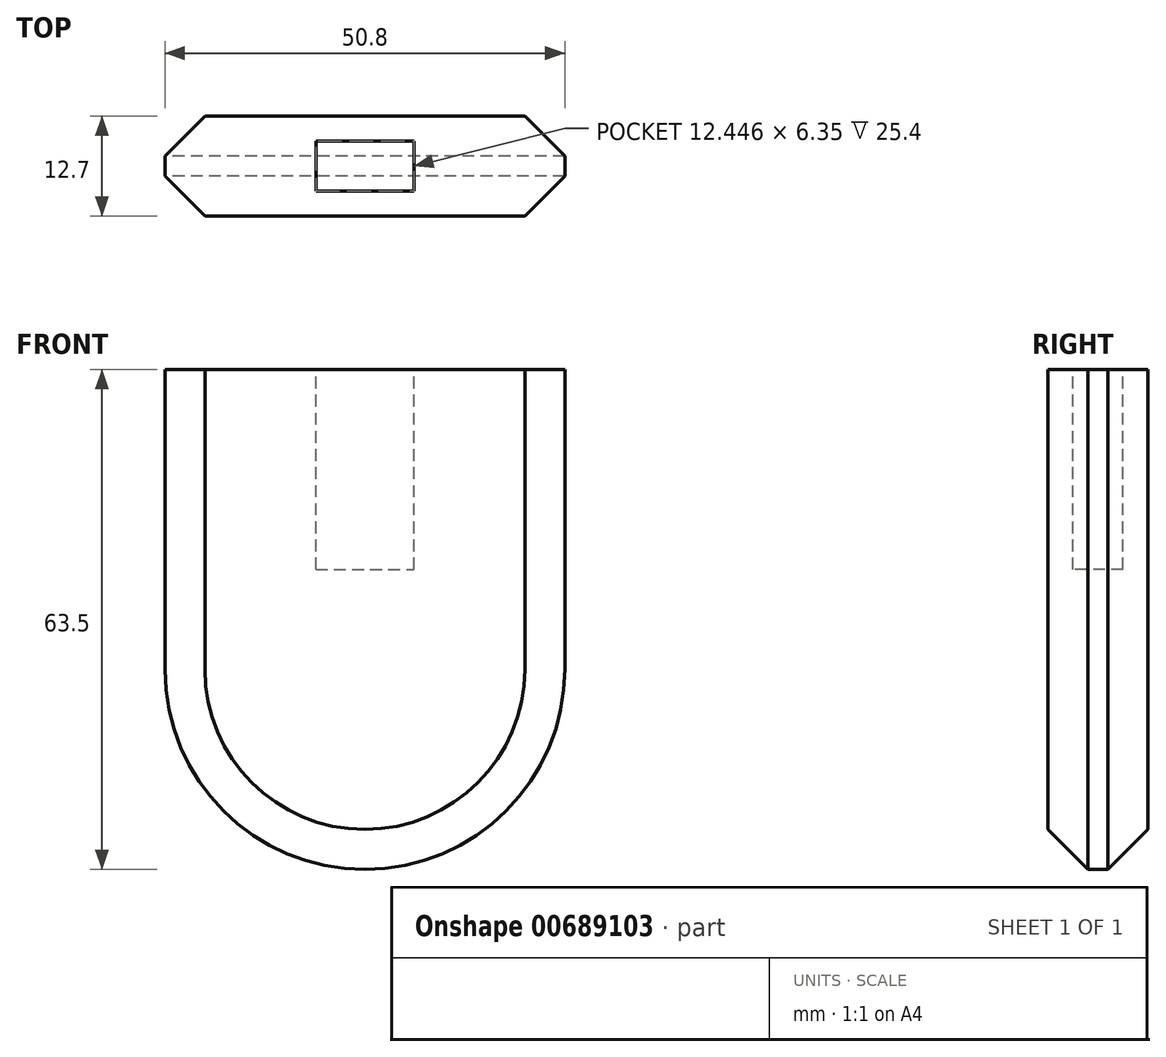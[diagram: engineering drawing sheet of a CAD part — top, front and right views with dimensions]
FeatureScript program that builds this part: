
annotation { "Feature Type Name" : "Feature", "Feature Type Description" : "" }
export const myFeature = defineFeature(function(context is Context, id is Id, definition is map)
    precondition{}
    {
        {
            var Q0;
            Q0=qCreatedBy(makeId("Top.planeOp"),FACE);
            var sketch = newSketch(context, id + "F0", { "sketchPlane" : qUnion([Q0])});
            skLineSegment(sketch, "E0.bottom", {"start": v(-25.4, 6.35) * mm, "end": v(25.4, 6.35) * mm});
            skLineSegment(sketch, "E0.top", {"start": v(-25.4, -6.35) * mm, "end": v(25.4, -6.35) * mm});
            skLineSegment(sketch, "E0.left", {"start": v(-25.4, 6.35) * mm, "end": v(-25.4, -6.35) * mm});
            skLineSegment(sketch, "E0.right", {"start": v(25.4, 6.35) * mm, "end": v(25.4, -6.35) * mm});
            skPoint(sketch, "E0.middle", {"position": v(0, 0) * mm});
            skSolve(sketch);
        }
        {
            var Q0;
            Q0 = qSketchRegion(id + "F0", true);
            extrude(context, id + "F1", {"entities" : qUnion([Q0]), "depth" : 25.4 * mm, "offsetDistance" : 25.4 * mm});
        }
        {
            var Q0;
            Q0 = qSketchRegion(id + "F0", true);
            extrude(context, id + "F2", {"entities" : qUnion([Q0]), "operationType" : NewBodyOperationType.ADD, "depth" : 63.5 * mm, "offsetDistance" : 25.4 * mm});
        }
        {
            var Q0;
            Q0=makeQuery(id+"F1.opExtrude","CAP_EDGE",EDGE,{"disambiguationData":[OSD([sQuery(id+"F0.wireOp",EDGE,"E0.right")])],"isStart":true});
            var Q1;
            Q1=makeQuery(id+"F1.opExtrude","CAP_EDGE",EDGE,{"disambiguationData":[OSD([sQuery(id+"F0.wireOp",EDGE,"E0.left")])],"isStart":true});
            fillet(context, id + "F3", {"entities" : qUnion([Q0, Q1]), "radius" : 25.4 * mm, "tangentPropagation" : true, "allowEdgeOverflow" : false});
        }
        {
            var Q0;
            {var subQ0=sQuery(id+"F0.wireOp",EDGE,"E0.top");Q0=makeQuery(id+"F3.opFillet","BLEND_EDGE",EDGE,{"blendedFrom":[makeQuery(id+"F1.opExtrude","CAP_EDGE",EDGE,{"disambiguationData":[OSD([sQuery(id+"F0.wireOp",EDGE,"E0.left")])],"isStart":true}),makeQuery(id+"F2.boolean.opBoolean","MERGE",FACE,{"derivedFrom":[makeQuery(id+"F1.opExtrude","SWEPT_FACE",FACE,{"disambiguationData":[OSD([subQ0])]}),makeQuery(id+"F2.opExtrude","SWEPT_FACE",FACE,{"disambiguationData":[OSD([subQ0])]})]})],"blendedInto":[makeQuery(id+"F2.boolean.opBoolean","MERGE",FACE,{"derivedFrom":[makeQuery(id+"F1.opExtrude","SWEPT_FACE",FACE,{"disambiguationData":[OSD([subQ0])]}),makeQuery(id+"F2.opExtrude","SWEPT_FACE",FACE,{"disambiguationData":[OSD([subQ0])]})]})]});}
            var Q1;
            {var subQ0=sQuery(id+"F0.wireOp",EDGE,"E0.bottom");Q1=makeQuery(id+"F3.opFillet","BLEND_EDGE",EDGE,{"blendedFrom":[makeQuery(id+"F1.opExtrude","CAP_EDGE",EDGE,{"disambiguationData":[OSD([sQuery(id+"F0.wireOp",EDGE,"E0.left")])],"isStart":true}),makeQuery(id+"F2.boolean.opBoolean","MERGE",FACE,{"derivedFrom":[makeQuery(id+"F1.opExtrude","SWEPT_FACE",FACE,{"disambiguationData":[OSD([subQ0])]}),makeQuery(id+"F2.opExtrude","SWEPT_FACE",FACE,{"disambiguationData":[OSD([subQ0])]})]})],"blendedInto":[makeQuery(id+"F2.boolean.opBoolean","MERGE",FACE,{"derivedFrom":[makeQuery(id+"F1.opExtrude","SWEPT_FACE",FACE,{"disambiguationData":[OSD([subQ0])]}),makeQuery(id+"F2.opExtrude","SWEPT_FACE",FACE,{"disambiguationData":[OSD([subQ0])]})]})]});}
            chamfer(context, id + "F4", {"entities" : qUnion([Q0, Q1]), "width" : 5.08 * mm, "tangentPropagation" : true});
        }
        {
            var Q0;
            Q0=makeQuery(id+"F2.opExtrude","CAP_FACE",FACE,{"disambiguationData":[OSD([sQuery(id+"F0.wireOp",EDGE,"E0.bottom"),sQuery(id+"F0.wireOp",EDGE,"E0.top"),sQuery(id+"F0.wireOp",EDGE,"E0.left"),sQuery(id+"F0.wireOp",EDGE,"E0.right")])],"isStart":false});
            var sketch = newSketch(context, id + "F5", { "sketchPlane" : qUnion([Q0])});
            skLineSegment(sketch, "E1.bottom", {"start": v(-6.22, 3.18) * mm, "end": v(6.22, 3.18) * mm});
            skLineSegment(sketch, "E1.top", {"start": v(-6.22, -3.18) * mm, "end": v(6.22, -3.18) * mm});
            skLineSegment(sketch, "E1.left", {"start": v(-6.22, 3.18) * mm, "end": v(-6.22, -3.18) * mm});
            skLineSegment(sketch, "E1.right", {"start": v(6.22, 3.18) * mm, "end": v(6.22, -3.18) * mm});
            skPoint(sketch, "E1.middle", {"position": v(0, 0) * mm});
            skSolve(sketch);
        }
        {
            var Q0;
            Q0 = qSketchRegion(id + "F5", true);
            extrude(context, id + "F6", {"entities" : qUnion([Q0]), "operationType" : NewBodyOperationType.REMOVE, "oppositeDirection" : true, "depth" : 25.4 * mm, "offsetDistance" : 25.4 * mm});
        }
    });
